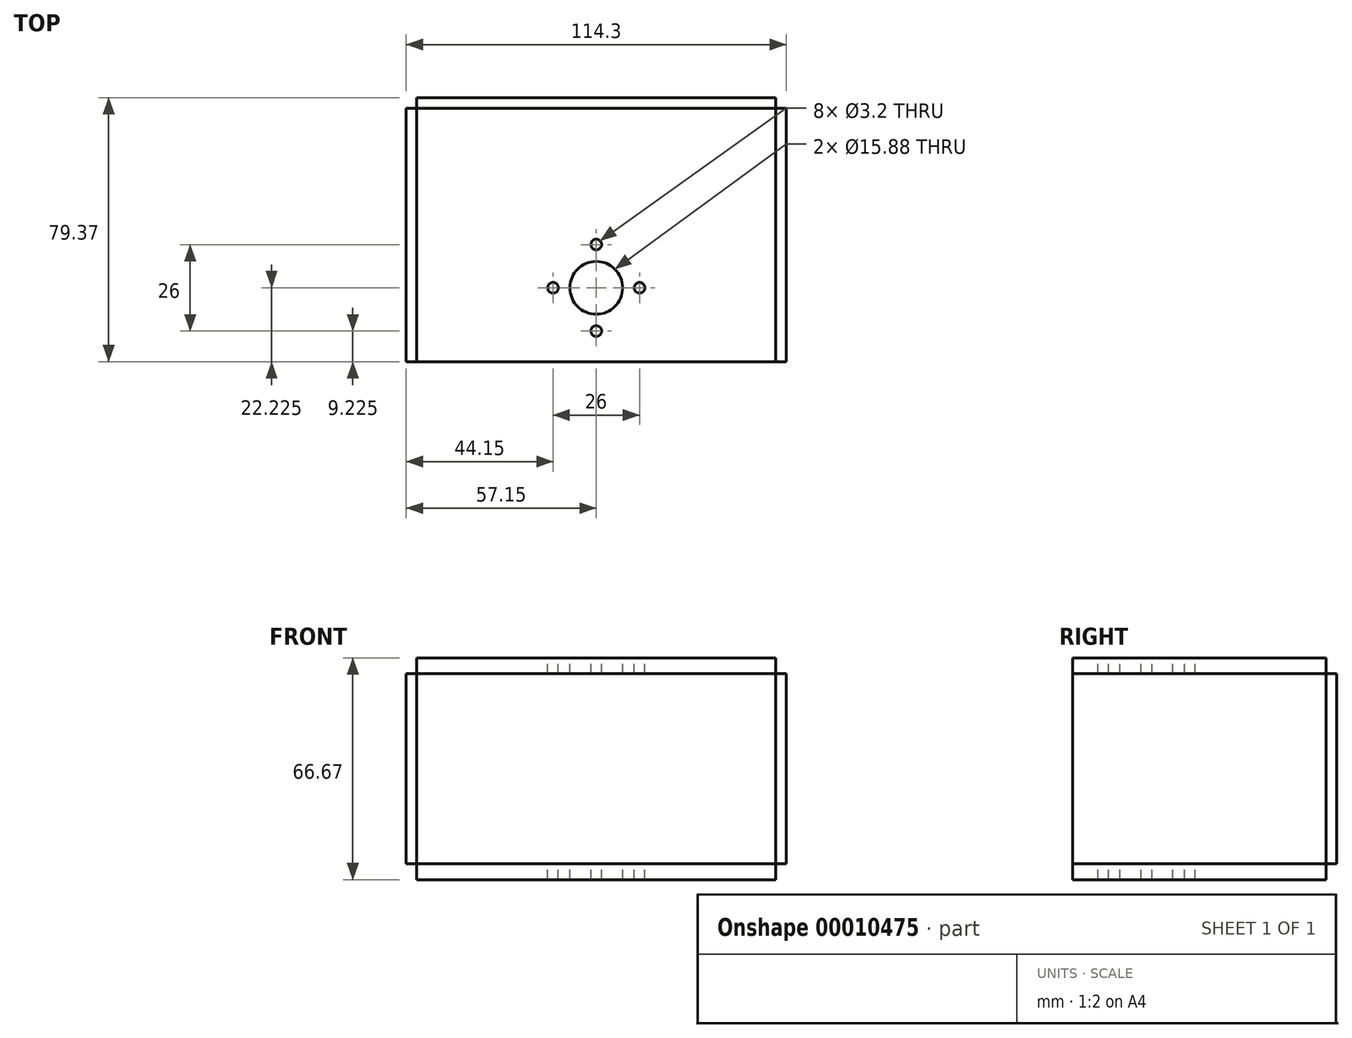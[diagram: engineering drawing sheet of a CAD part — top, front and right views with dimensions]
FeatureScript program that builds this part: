
annotation { "Feature Type Name" : "Feature", "Feature Type Description" : "" }
export const myFeature = defineFeature(function(context is Context, id is Id, definition is map)
    precondition{}
    {
        {
            var Q0;
            Q0=qCreatedBy(makeId("Top.planeOp"),FACE);
            var sketch = newSketch(context, id + "F0", { "sketchPlane" : qUnion([Q0])});
            skLineSegment(sketch, "E0.rect.bottom", {"start": v(53.97, 38.1) * mm, "end": v(-53.98, 38.1) * mm});
            skLineSegment(sketch, "E0.rect.top", {"start": v(53.98, -38.1) * mm, "end": v(-53.97, -38.1) * mm});
            skLineSegment(sketch, "E0.rect.left", {"start": v(53.97, 38.1) * mm, "end": v(53.98, -38.1) * mm});
            skLineSegment(sketch, "E0.rect.right", {"start": v(-53.98, 38.1) * mm, "end": v(-53.97, -38.1) * mm});
            skPoint(sketch, "E0.rect.middle", {"position": v(0, 0) * mm});
            skSolve(sketch);
        }
        {
            var Q0;
            Q0 = qSketchRegion(id + "F0", true);
            extrude(context, id + "F1", {"entities" : qUnion([Q0]), "depth" : 4.76 * mm});
        }
        {
            var Q0;
            Q0=makeQuery(id+"F1.opExtrude","SWEPT_FACE",FACE,{"disambiguationData":[OSD([sQuery(id+"F0.wireOp",EDGE,"E0.rect.bottom")])]});
            var sketch = newSketch(context, id + "F2", { "sketchPlane" : qUnion([Q0])});
            skLineSegment(sketch, "E1.bottom", {"start": v(53.98, 0) * mm, "end": v(-53.97, 0) * mm});
            skLineSegment(sketch, "E1.top", {"start": v(53.98, -57.15) * mm, "end": v(-53.97, -57.15) * mm});
            skLineSegment(sketch, "E1.left", {"start": v(53.98, 0) * mm, "end": v(53.98, -57.15) * mm});
            skLineSegment(sketch, "E1.right", {"start": v(-53.97, 0) * mm, "end": v(-53.97, -57.15) * mm});
            skSolve(sketch);
        }
        {
            var Q0;
            Q0 = qSketchRegion(id + "F2", true);
            extrude(context, id + "F3", {"entities" : qUnion([Q0]), "depth" : 3.17 * mm});
        }
        {
            var Q0;
            Q0=makeQuery(id+"F1.opExtrude","SWEPT_FACE",FACE,{"disambiguationData":[OSD([sQuery(id+"F0.wireOp",EDGE,"E0.rect.left")])]});
            var sketch = newSketch(context, id + "F4", { "sketchPlane" : qUnion([Q0])});
            skLineSegment(sketch, "E2.bottom", {"start": v(38.1, 0) * mm, "end": v(-38.1, 0) * mm});
            skLineSegment(sketch, "E2.top", {"start": v(38.1, -57.15) * mm, "end": v(-38.1, -57.15) * mm});
            skLineSegment(sketch, "E2.left", {"start": v(38.1, 0) * mm, "end": v(38.1, -57.15) * mm});
            skLineSegment(sketch, "E2.right", {"start": v(-38.1, 0) * mm, "end": v(-38.1, -57.15) * mm});
            skSolve(sketch);
        }
        {
            var Q0;
            Q0 = qSketchRegion(id + "F4", true);
            extrude(context, id + "F5", {"entities" : qUnion([Q0]), "depth" : 3.17 * mm});
        }
        {
            var Q0;
            Q0=makeQuery(id+"F5.opExtrude","SWEPT_FACE",FACE,{"disambiguationData":[OSD([sQuery(id+"F4.wireOp",EDGE,"E2.top")])]});
            var sketch = newSketch(context, id + "F6", { "sketchPlane" : qUnion([Q0])});
            skLineSegment(sketch, "E3.bottom", {"start": v(53.97, -38.1) * mm, "end": v(-53.98, -38.1) * mm});
            skLineSegment(sketch, "E3.top", {"start": v(53.98, 38.1) * mm, "end": v(-53.98, 38.1) * mm});
            skLineSegment(sketch, "E3.left", {"start": v(53.97, -38.1) * mm, "end": v(53.97, 38.1) * mm});
            skLineSegment(sketch, "E3.right", {"start": v(-53.98, -38.1) * mm, "end": v(-53.98, 38.1) * mm});
            skSolve(sketch);
        }
        {
            var Q0;
            Q0 = qSketchRegion(id + "F6", true);
            extrude(context, id + "F7", {"entities" : qUnion([Q0]), "depth" : 4.76 * mm});
        }
        {
            var Q0;
            Q0=makeQuery(id+"F1.opExtrude","SWEPT_FACE",FACE,{"disambiguationData":[OSD([sQuery(id+"F0.wireOp",EDGE,"E0.rect.right")])]});
            var sketch = newSketch(context, id + "F8", { "sketchPlane" : qUnion([Q0])});
            skLineSegment(sketch, "E4.bottom", {"start": v(-38.1, 0) * mm, "end": v(38.1, 0) * mm});
            skLineSegment(sketch, "E4.top", {"start": v(-38.1, -57.15) * mm, "end": v(38.1, -57.15) * mm});
            skLineSegment(sketch, "E4.left", {"start": v(-38.1, 0) * mm, "end": v(-38.1, -57.15) * mm});
            skLineSegment(sketch, "E4.right", {"start": v(38.1, 0) * mm, "end": v(38.1, -57.15) * mm});
            skSolve(sketch);
        }
        {
            var Q0;
            Q0 = qSketchRegion(id + "F8", true);
            extrude(context, id + "F9", {"entities" : qUnion([Q0]), "depth" : 3.17 * mm});
        }
        {
            var Q0;
            Q0=makeQuery(id+"F1.opExtrude","CAP_FACE",FACE,{"disambiguationData":[OSD([sQuery(id+"F0.wireOp",EDGE,"E0.rect.bottom"),sQuery(id+"F0.wireOp",EDGE,"E0.rect.top"),sQuery(id+"F0.wireOp",EDGE,"E0.rect.left"),sQuery(id+"F0.wireOp",EDGE,"E0.rect.right")])],"isStart":false});
            var sketch = newSketch(context, id + "F10", { "sketchPlane" : qUnion([Q0])});
            skLineSegment(sketch, "E5", {"start": v(0, -38.1) * mm, "end": v(0, 38.1) * mm, "construction": true});
            skCircle(sketch, "E6", {"center": v(0, -15.88) * mm, "radius": 7.94 * mm});
            skCircle(sketch, "E7", {"center": v(0, -15.88) * mm, "radius": 13 * mm, "construction": true});
            skCircle(sketch, "E8", {"center": v(13, -15.88) * mm, "radius": 1.6 * mm});
            skCircle(sketch, "E9.1.0", {"center": v(0, -2.88) * mm, "radius": 1.6 * mm});
            skCircle(sketch, "E9.2.0", {"center": v(-13, -15.88) * mm, "radius": 1.6 * mm});
            skCircle(sketch, "E9.3.0", {"center": v(0, -28.87) * mm, "radius": 1.6 * mm});
            skSolve(sketch);
        }
        {
            var Q0;
            Q0 = qSketchRegion(id + "F10", true);
            extrude(context, id + "F11", {"entities" : qUnion([Q0]), "operationType" : NewBodyOperationType.REMOVE, "endBound" : BoundingType.THROUGH_ALL, "oppositeDirection" : true, "depth" : 25 * mm});
        }
        {
            var Q0;
            Q0=makeQuery(id+"F7.opExtrude","CAP_FACE",FACE,{"disambiguationData":[OSD([sQuery(id+"F6.wireOp",EDGE,"E3.bottom"),sQuery(id+"F6.wireOp",EDGE,"E3.top"),sQuery(id+"F6.wireOp",EDGE,"E3.left"),sQuery(id+"F6.wireOp",EDGE,"E3.right")])],"isStart":true});
            var sketch = newSketch(context, id + "F12", { "sketchPlane" : qUnion([Q0])});
            skLineSegment(sketch, "E10", {"start": v(0, 38.1) * mm, "end": v(0, -38.1) * mm, "construction": true});
            skCircle(sketch, "E11", {"center": v(0, -15.87) * mm, "radius": 7.94 * mm});
            skCircle(sketch, "E12", {"center": v(0, -15.87) * mm, "radius": 13 * mm, "construction": true});
            skCircle(sketch, "E13", {"center": v(13, -15.87) * mm, "radius": 1.6 * mm});
            skCircle(sketch, "E14.1.0", {"center": v(0, -2.87) * mm, "radius": 1.6 * mm});
            skCircle(sketch, "E14.2.0", {"center": v(-13, -15.87) * mm, "radius": 1.6 * mm});
            skCircle(sketch, "E14.3.0", {"center": v(0, -28.87) * mm, "radius": 1.6 * mm});
            skSolve(sketch);
        }
        {
            var Q0;
            Q0 = qSketchRegion(id + "F12", true);
            extrude(context, id + "F13", {"entities" : qUnion([Q0]), "operationType" : NewBodyOperationType.REMOVE, "endBound" : BoundingType.THROUGH_ALL, "oppositeDirection" : true, "depth" : 25.4 * mm});
        }
    });
